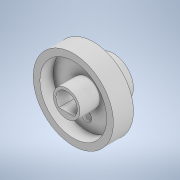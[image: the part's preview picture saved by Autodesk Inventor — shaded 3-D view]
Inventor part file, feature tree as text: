
AUTODESK INVENTOR PART (.ipt)
format: ipt  version: 2021 (Build 250183000, 183)  size: 182,272 bytes
history: native  units: mm
features: projected_geometry x9, extrude x6, sketch x6, reference x4, other x4, direct_edit x3, move_body x3
ambient origin geometry x8: Origin, YZ Plane, XZ Plane, XY Plane, X Axis, Y Axis, Z Axis, Center Point
bodies: Solid1 (feature_tree)
feature tree (35):
  extrude  "Extrusion1"  Depth=4.0mm
  extrude  "Extrusion2"  Depth=2.5mm
  extrude  "Extrusion3"  Depth=6.0mm
  extrude  "Extrusion4"  Depth=3.0mm TaperAngle=0.0deg
  extrude  "Extrusion5"  Depth=1.0mm TaperAngle=0.0deg
  extrude  "Extrusion6"  Depth=1.8mm TaperAngle=0.0deg
  direct_edit  "Direct Edit1"
  direct_edit  "Direct Edit2"
  direct_edit  "Direct Edit3"
  sketch  "Sketch1"  dims[d0=0.1mm d1=4.0mm]
  reference  "Reference1"
  reference  "Reference2"
  reference  "Reference3"
  reference  "Reference4"
  sketch  "Sketch2"  dims[d2=2.5mm d3=0.0mm d4=12.0mm]
  projected_geometry  "Projected Loop1"
  sketch  "Sketch3"  dims[d5=1.5mm d6=0.0mm d7=6.0mm]
  projected_geometry  "Projected Loop2"
  sketch  "Sketch4"  dims[d8=3.0mm d9=0.0mm d10=1.5mm d11=0.0mm]
  projected_geometry  "Projected Loop3"
  projected_geometry  "Projected Loop4"
  sketch  "Sketch5"  dims[d12=1.0mm d13=1.5mm d14=0.0mm]
  projected_geometry  "Projected Loop5"
  projected_geometry  "Projected Loop6"
  sketch  "Sketch6"  dims[d16=1.5mm d17=1.8mm d18=0.0mm d25=0.6mm d26=0.0mm d27=0.0mm d28=-1.0mm d29=0.0mm d30=0.0mm d31=-0.5mm d32=0.0mm d33=0.0mm d34=-1.5mm]
  projected_geometry  "Projected Loop7"
  projected_geometry  "Projected Loop8"
  projected_geometry  "Projected Loop9"
  parser-record x1  (decoder bookkeeping rows leaked as tree rows — omitted from the tree; the rows remain in map.json)
  other  "motorCaseEpn.iam"
  other  "GearMotor:1"
  other  "Eixo - Encaixe D:1"
  move_body  "Move1"
  move_body  "Move2"
  move_body  "Move3"
note: 1 file-system path scrubbed to <path> (originals preserved in map.json)
